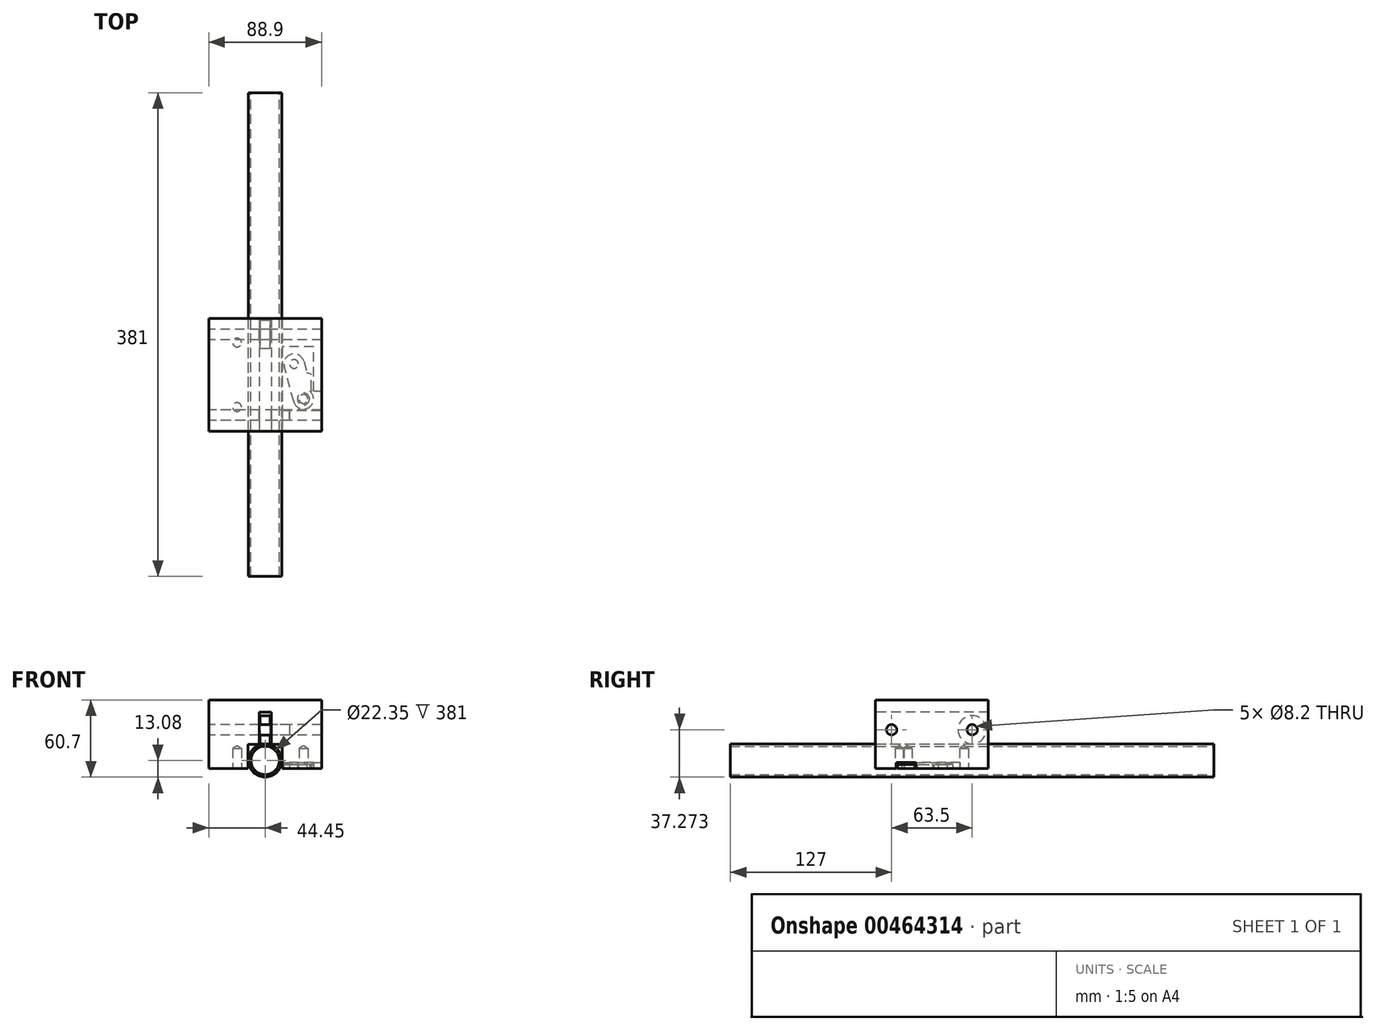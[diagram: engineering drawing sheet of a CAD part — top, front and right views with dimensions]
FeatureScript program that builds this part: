
annotation { "Feature Type Name" : "Feature", "Feature Type Description" : "" }
export const myFeature = defineFeature(function(context is Context, id is Id, definition is map)
    precondition{}
    {
        {
            var Q0;
            Q0=qCreatedBy(makeId("Front.planeOp"),FACE);
            var sketch = newSketch(context, id + "F0", { "sketchPlane" : qUnion([Q0])});
            skCircle(sketch, "E0", {"center": v(0, 0) * mm, "radius": 13.08 * mm});
            skCircle(sketch, "E1", {"center": v(0, 0) * mm, "radius": 11.18 * mm});
            skLineSegment(sketch, "E2.bottom", {"start": v(-3.94, 13.08) * mm, "end": v(3.94, 13.08) * mm});
            skLineSegment(sketch, "E2.top", {"start": v(-3.94, 20.13) * mm, "end": v(3.94, 20.13) * mm});
            skLineSegment(sketch, "E2.left", {"start": v(-3.94, 13.08) * mm, "end": v(-3.94, 20.13) * mm});
            skLineSegment(sketch, "E2.right", {"start": v(3.94, 13.08) * mm, "end": v(3.94, 20.13) * mm});
            skLineSegment(sketch, "E3", {"start": v(-8.64, 24.2) * mm, "end": v(7.29, 24.2) * mm, "construction": true});
            skLineSegment(sketch, "E4", {"start": v(0, 13.08) * mm, "end": v(0, 0) * mm, "construction": true});
            skSolve(sketch);
        }
        {
            var Q0;
            Q0=makeQuery(id+"F0.imprint","IMPRINT",FACE,{"disambiguationData":[TD([[makeQuery(id+"F0.imprint","IMPRINT",EDGE,{"derivedFrom":sQuery(id+"F0.wireOp",EDGE,"E0")}),1.0]])]});
            extrude(context, id + "F1", {"entities" : qUnion([Q0]), "depth" : 381 * mm, "symmetric" : true});
        }
        {
            var Q0;
            Q0=makeQuery(id+"F0.imprint","IMPRINT",FACE,{"disambiguationData":[TD([[makeQuery(id+"F0.imprint","IMPRINT",EDGE,{"derivedFrom":sQuery(id+"F0.wireOp",EDGE,"E2.top")}),-1.0]])]});
            var Q1;
            Q1=sQuery(id+"F0.wireOp",EDGE,"E3");
            revolve(context, id + "F2", {"entities" : qUnion([Q0]), "axis" : qUnion([Q1]), "revolveType" : RevolveType.FULL});
        }
        {
            var Q0;
            Q0=qCreatedBy(makeId("Front.planeOp"),FACE);
            var sketch = newSketch(context, id + "F3", { "sketchPlane" : qUnion([Q0])});
            skLineSegment(sketch, "E5.bottom", {"start": v(-44.45, -6.35) * mm, "end": v(44.45, -6.35) * mm});
            skLineSegment(sketch, "E5.top", {"start": v(-44.45, 47.62) * mm, "end": v(44.45, 47.62) * mm});
            skLineSegment(sketch, "E5.left", {"start": v(-44.45, -6.35) * mm, "end": v(-44.45, 47.63) * mm});
            skLineSegment(sketch, "E5.right", {"start": v(44.45, -6.35) * mm, "end": v(44.45, 47.63) * mm});
            skLineSegment(sketch, "E6.bottom", {"start": v(-4.76, 38.1) * mm, "end": v(4.76, 38.1) * mm});
            skLineSegment(sketch, "E6.top", {"start": v(-4.76, 0) * mm, "end": v(4.76, 0) * mm});
            skLineSegment(sketch, "E6.left", {"start": v(-4.76, 38.1) * mm, "end": v(-4.76, 0) * mm});
            skLineSegment(sketch, "E6.right", {"start": v(4.76, 38.1) * mm, "end": v(4.76, 0) * mm});
            skLineSegment(sketch, "E7.bottom", {"start": v(-13.46, 12.7) * mm, "end": v(13.46, 12.7) * mm});
            skLineSegment(sketch, "E7.top", {"start": v(-13.46, -14.22) * mm, "end": v(13.46, -14.22) * mm});
            skLineSegment(sketch, "E7.left", {"start": v(-13.46, 12.7) * mm, "end": v(-13.46, -14.22) * mm});
            skLineSegment(sketch, "E7.right", {"start": v(13.46, 12.7) * mm, "end": v(13.46, -14.22) * mm});
            skLineSegment(sketch, "E8", {"start": v(0, 47.62) * mm, "end": v(0, 0) * mm, "construction": true});
            skCircle(sketch, "E9.0", {"center": v(0, 0) * mm, "radius": 13.08 * mm});
            skLineSegment(sketch, "E10.bottom", {"start": v(-10.98, -7.11) * mm, "end": v(-33.2, -7.11) * mm});
            skLineSegment(sketch, "E10.top", {"start": v(-10.98, -14.99) * mm, "end": v(-33.2, -14.99) * mm});
            skLineSegment(sketch, "E10.left", {"start": v(-10.98, -7.11) * mm, "end": v(-10.98, -14.99) * mm});
            skLineSegment(sketch, "E10.right", {"start": v(-33.2, -7.11) * mm, "end": v(-33.2, -14.99) * mm});
            skLineSegment(sketch, "E11", {"start": v(-22.1, -14.99) * mm, "end": v(-22.1, 0) * mm, "construction": true});
            skSolve(sketch);
        }
        {
            var Q0;
            Q0=makeQuery(id+"F3.imprint","IMPRINT",FACE,{"disambiguationData":[TD([[makeQuery(id+"F3.imprint","IMPRINT",EDGE,{"derivedFrom":sQuery(id+"F3.wireOp",EDGE,"E5.top")}),-1.0]])]});
            extrude(context, id + "F4", {"entities" : qUnion([Q0]), "oppositeDirection" : true, "depth" : 12.7 * mm, "hasSecondDirection" : true, "secondDirectionOppositeDirection" : false, "secondDirectionDepth" : 76.2 * mm});
        }
        {
            var Q0;
            {var subQ0=sQuery(id+"F3.wireOp",EDGE,"E5.bottom");Q0=makeQuery(id+"F4.opExtrude","SWEPT_FACE",FACE,{"disambiguationData":[OSD([subQ0]),TDD([makeQuery(id+"F3.imprint","IMPRINT",EDGE,{"disambiguationData":[TD([[makeQuery(id+"F3.imprint","INTERSECT",VERTEX,{"derivedFrom":[subQ0,sQuery(id+"F3.wireOp",EDGE,"E5.left")]}),-1.0]])],"derivedFrom":subQ0})])]});}
            var sketch = newSketch(context, id + "F5", { "sketchPlane" : qUnion([Q0])});
            skPoint(sketch, "E12.0", {"position": v(-22.1, 0) * mm});
            skLineSegment(sketch, "E13", {"start": v(-22.1, 0) * mm, "end": v(-22.1, 57.15) * mm, "construction": true});
            skPoint(sketch, "E14", {"position": v(-22.1, 57.15) * mm});
            skPoint(sketch, "E15", {"position": v(-22.1, 6.35) * mm});
            skLineSegment(sketch, "E16.0", {"start": v(-44.45, 76.2) * mm, "end": v(-13.46, 76.2) * mm});
            skLineSegment(sketch, "E17.0", {"start": v(-44.45, -12.7) * mm, "end": v(-44.45, 76.2) * mm});
            skPoint(sketch, "E18", {"position": v(30.18, 50.8) * mm});
            skSolve(sketch);
        }
        {
            var Q0;
            Q0=sQuery(id+"F5.wireOp",VERTEX,"E14");
            var Q1;
            Q1=sQuery(id+"F5.wireOp",VERTEX,"E15");
            var Q2;
            Q2=sQuery(id+"F5.wireOp",VERTEX,"E18");
            var Q3;
            Q3=makeQuery(id+"F4.opExtrude","SWEPT_BODY",BODY,{"disambiguationData":[OSD([sQuery(id+"F3.wireOp",EDGE,"E5.bottom"),sQuery(id+"F3.wireOp",EDGE,"E5.top"),sQuery(id+"F3.wireOp",EDGE,"E5.left"),sQuery(id+"F3.wireOp",EDGE,"E5.right"),sQuery(id+"F3.wireOp",EDGE,"E6.bottom"),sQuery(id+"F3.wireOp",EDGE,"E6.left"),sQuery(id+"F3.wireOp",EDGE,"E6.right"),sQuery(id+"F3.wireOp",EDGE,"E7.bottom"),sQuery(id+"F3.wireOp",EDGE,"E7.left"),sQuery(id+"F3.wireOp",EDGE,"E7.right")])]});
            hole(context, id + "F6", {"style" : HoleStyle.SIMPLE, "endStyle" : HoleEndStyle.BLIND, "standardTappedOrClearance" : lookupTablePath({ "standard" : "ANSI", "engagement" : "75%", "pitch" : "24 tpi", "size" : "5/16", "type" : "Tapped" }), "standardBlindInLast" : lookupTablePath({ "standard" : "ANSI", "engagement" : "75%", "pitch" : "24 tpi", "size" : "5/16", "type" : "Tapped" }), "holeDiameter" : 6.9 * mm, "showTappedDepth" : true, "holeDepth" : 15.88 * mm, "isTappedThrough" : true, "tappedDepth" : 12.7 * mm, "tapClearance" : 3, "startFromSketch" : true, "locations" : qUnion([Q0, Q1, Q2]), "scope" : qUnion([Q3]), "majorDiameter" : 7.94 * mm});
        }
        {
            var Q0;
            Q0=makeQuery(id+"F4.opExtrude","SWEPT_FACE",FACE,{"disambiguationData":[OSD([sQuery(id+"F3.wireOp",EDGE,"E5.left")])]});
            var sketch = newSketch(context, id + "F7", { "sketchPlane" : qUnion([Q0])});
            skPoint(sketch, "E19.0", {"position": v(0, 24.2) * mm});
            skLineSegment(sketch, "E20", {"start": v(0, 24.2) * mm, "end": v(63.5, 24.2) * mm});
            skPoint(sketch, "E21", {"position": v(63.5, 24.2) * mm});
            skSolve(sketch);
        }
        {
            var Q0;
            Q0=sQuery(id+"F7.wireOp",VERTEX,"E19.0");
            var Q1;
            Q1=sQuery(id+"F7.wireOp",VERTEX,"E21");
            var Q2;
            Q2=makeQuery(id+"F4.opExtrude","SWEPT_BODY",BODY,{"disambiguationData":[OSD([sQuery(id+"F3.wireOp",EDGE,"E5.bottom"),sQuery(id+"F3.wireOp",EDGE,"E5.top"),sQuery(id+"F3.wireOp",EDGE,"E5.left"),sQuery(id+"F3.wireOp",EDGE,"E5.right"),sQuery(id+"F3.wireOp",EDGE,"E6.bottom"),sQuery(id+"F3.wireOp",EDGE,"E6.left"),sQuery(id+"F3.wireOp",EDGE,"E6.right"),sQuery(id+"F3.wireOp",EDGE,"E7.bottom"),sQuery(id+"F3.wireOp",EDGE,"E7.left"),sQuery(id+"F3.wireOp",EDGE,"E7.right")])]});
            var Q3;
            Q3=makeQuery(id+"F2.opRevolve","SWEPT_BODY",BODY,{"disambiguationData":[OSD([sQuery(id+"F0.wireOp",EDGE,"E2.bottom"),sQuery(id+"F0.wireOp",EDGE,"E2.top"),sQuery(id+"F0.wireOp",EDGE,"E2.left"),sQuery(id+"F0.wireOp",EDGE,"E2.right")])]});
            hole(context, id + "F8", {"style" : HoleStyle.SIMPLE, "endStyle" : HoleEndStyle.THROUGH, "standardTappedOrClearance" : lookupTablePath({ "standard" : "ANSI", "fit" : "Close", "size" : "5/16", "type" : "Clearance" }), "standardBlindInLast" : lookupTablePath({ "fit" : "Close", "standard" : "ANSI", "size" : "5/16", "type" : "Clearance" }), "holeDiameter" : 8.2 * mm, "isTappedThrough" : true, "tappedDepth" : 12.7 * mm, "tapClearance" : 3, "startFromSketch" : true, "locations" : qUnion([Q0, Q1]), "scope" : qUnion([Q2, Q3])});
        }
        {
            var Q0;
            Q0=makeQuery(id+"F4.opExtrude","SWEPT_FACE",FACE,{"disambiguationData":[OSD([sQuery(id+"F3.wireOp",EDGE,"E5.left")])]});
            var sketch = newSketch(context, id + "F9", { "sketchPlane" : qUnion([Q0])});
            skCircle(sketch, "E22.0", {"center": v(63.5, 24.2) * mm, "radius": 4.1 * mm});
            skSolve(sketch);
        }
        {
            var Q0;
            Q0=makeQuery(id+"F9.imprint","IMPRINT",FACE,{"disambiguationData":[TD([[makeQuery(id+"F9.imprint","IMPRINT",EDGE,{"derivedFrom":sQuery(id+"F9.wireOp",EDGE,"E22.0")}),1.0]])]});
            extrude(context, id + "F10", {"entities" : qUnion([Q0]), "oppositeDirection" : true, "depth" : 63.5 * mm});
        }
        {
            var Q0;
            {var subQ0=sQuery(id+"F3.wireOp",EDGE,"E5.bottom");Q0=makeQuery(id+"F4.opExtrude","SWEPT_FACE",FACE,{"disambiguationData":[OSD([subQ0]),TDD([makeQuery(id+"F3.imprint","IMPRINT",EDGE,{"disambiguationData":[TD([[makeQuery(id+"F3.imprint","INTERSECT",VERTEX,{"derivedFrom":[subQ0,sQuery(id+"F3.wireOp",EDGE,"E5.right")]}),1.0]])],"derivedFrom":subQ0})])]});}
            var sketch = newSketch(context, id + "F11", { "sketchPlane" : qUnion([Q0])});
            skCircle(sketch, "E23.0", {"center": v(30.18, 50.8) * mm, "radius": 3.45 * mm});
            skCircle(sketch, "E24", {"center": v(30.18, 50.8) * mm, "radius": 4.76 * mm});
            skCircle(sketch, "E25", {"center": v(30.18, 50.8) * mm, "radius": 7.94 * mm});
            skCircle(sketch, "E26", {"center": v(22.78, 23.2) * mm, "radius": 3.45 * mm});
            skCircle(sketch, "E27", {"center": v(22.78, 23.2) * mm, "radius": 7.94 * mm});
            skLineSegment(sketch, "E28", {"start": v(22.5, 52.85) * mm, "end": v(15.11, 25.25) * mm});
            skLineSegment(sketch, "E29", {"start": v(30.45, 21.14) * mm, "end": v(37.84, 48.75) * mm});
            skLineSegment(sketch, "E30", {"start": v(36.39, 43.31) * mm, "end": v(36.39, 31.04) * mm});
            skLineSegment(sketch, "E31", {"start": v(36.39, 31.04) * mm, "end": v(32.84, 30.1) * mm});
            skLineSegment(sketch, "E32", {"start": v(37.84, 48.75) * mm, "end": v(39.21, 48.38) * mm, "construction": true});
            skLineSegment(sketch, "E33.0.0", {"start": v(44.45, 76.2) * mm, "end": v(13.46, 76.2) * mm});
            skLineSegment(sketch, "E33.0.1", {"start": v(13.46, 76.2) * mm, "end": v(13.46, -12.7) * mm});
            skLineSegment(sketch, "E33.0.2", {"start": v(13.46, -12.7) * mm, "end": v(44.45, -12.7) * mm});
            skLineSegment(sketch, "E33.0.3", {"start": v(44.45, -12.7) * mm, "end": v(44.45, 76.2) * mm});
            skLineSegment(sketch, "E34.bottom", {"start": v(13.46, 59.69) * mm, "end": v(44.45, 59.69) * mm});
            skLineSegment(sketch, "E34.top", {"start": v(13.46, 44.45) * mm, "end": v(44.45, 44.45) * mm});
            skLineSegment(sketch, "E34.left", {"start": v(13.46, 59.7) * mm, "end": v(13.46, 44.45) * mm});
            skLineSegment(sketch, "E34.right", {"start": v(44.45, 59.69) * mm, "end": v(44.45, 44.45) * mm});
            skLineSegment(sketch, "E35.bottom", {"start": v(38.1, 44.45) * mm, "end": v(13.46, 44.45) * mm});
            skLineSegment(sketch, "E35.top", {"start": v(38.1, 9.52) * mm, "end": v(13.46, 9.52) * mm});
            skLineSegment(sketch, "E35.left", {"start": v(38.1, 44.45) * mm, "end": v(38.1, 9.52) * mm});
            skLineSegment(sketch, "E35.right", {"start": v(13.46, 44.45) * mm, "end": v(13.46, 9.52) * mm});
            skSolve(sketch);
        }
        {
            var Q0;
            Q0=makeQuery(id+"F11.imprint","IMPRINT",FACE,{"disambiguationData":[TD([[makeQuery(id+"F11.imprint","IMPRINT",EDGE,{"derivedFrom":sQuery(id+"F11.wireOp",EDGE,"E34.bottom")}),-1.0]])]});
            var Q1;
            Q1=makeQuery(id+"F11.imprint","IMPRINT",FACE,{"disambiguationData":[TD([[makeQuery(id+"F11.imprint","IMPRINT",EDGE,{"derivedFrom":sQuery(id+"F11.wireOp",EDGE,"E24")}),-1.0]])]});
            var Q2;
            {var subQ0=sQuery(id+"F11.wireOp",EDGE,"E28");var subQ1=sQuery(id+"F11.wireOp",EDGE,"E25");var subQ2=makeQuery(id+"F11.imprint","INTERSECT",VERTEX,{"derivedFrom":[subQ1,subQ0]});Q2=makeQuery(id+"F11.imprint","IMPRINT",FACE,{"disambiguationData":[TD([[makeQuery(id+"F11.imprint","IMPRINT",EDGE,{"disambiguationData":[TD([[subQ2,-1.0]])],"derivedFrom":subQ1}),-1.0]])]});}
            var Q3;
            {var subQ0=sQuery(id+"F11.wireOp",EDGE,"E29");var subQ1=sQuery(id+"F11.wireOp",EDGE,"E25");var subQ2=makeQuery(id+"F11.imprint","INTERSECT",VERTEX,{"derivedFrom":[subQ1,subQ0]});Q3=makeQuery(id+"F11.imprint","IMPRINT",FACE,{"disambiguationData":[TD([[makeQuery(id+"F11.imprint","IMPRINT",EDGE,{"disambiguationData":[TD([[subQ2,1.0]])],"derivedFrom":subQ1}),-1.0]])]});}
            var Q4;
            {var subQ6=sQuery(id+"F11.wireOp",EDGE,"E35.bottom");var subQ8=sQuery(id+"F11.wireOp",EDGE,"E25");var subQ9=makeQuery(id+"F11.imprint","INTERSECT",VERTEX,{"disambiguationData":[OD(0.0)],"derivedFrom":[subQ8,subQ6]});Q4=makeQuery(id+"F11.imprint","IMPRINT",FACE,{"disambiguationData":[TD([[makeQuery(id+"F11.imprint","IMPRINT",EDGE,{"disambiguationData":[TD([[subQ9,-1.0]])],"derivedFrom":subQ8}),-1.0]])]});}
            var Q5;
            {var subQ0=sQuery(id+"F11.wireOp",EDGE,"E35.bottom");var subQ1=sQuery(id+"F11.wireOp",EDGE,"E25");var subQ2=makeQuery(id+"F11.imprint","INTERSECT",VERTEX,{"disambiguationData":[OD(0.0)],"derivedFrom":[subQ1,subQ0]});Q5=makeQuery(id+"F11.imprint","IMPRINT",FACE,{"disambiguationData":[TD([[makeQuery(id+"F11.imprint","IMPRINT",EDGE,{"disambiguationData":[TD([[subQ2,-1.0]])],"derivedFrom":subQ1}),1.0]])]});}
            var Q6;
            {var subQ0=sQuery(id+"F11.wireOp",EDGE,"E30");Q6=makeQuery(id+"F11.imprint","IMPRINT",FACE,{"disambiguationData":[TD([[makeQuery(id+"F11.imprint","IMPRINT",EDGE,{"derivedFrom":subQ0}),-1.0]])]});}
            var Q7;
            {var subQ8=sQuery(id+"F11.wireOp",EDGE,"E30");Q7=makeQuery(id+"F11.imprint","IMPRINT",FACE,{"disambiguationData":[TD([[makeQuery(id+"F11.imprint","IMPRINT",EDGE,{"derivedFrom":subQ8}),1.0]])]});}
            var Q8;
            Q8=makeQuery(id+"F11.imprint","IMPRINT",FACE,{"disambiguationData":[TD([[makeQuery(id+"F11.imprint","IMPRINT",EDGE,{"derivedFrom":sQuery(id+"F11.wireOp",EDGE,"E26")}),-1.0]])]});
            var Q9;
            Q9=makeQuery(id+"F11.imprint","IMPRINT",FACE,{"disambiguationData":[TD([[makeQuery(id+"F11.imprint","IMPRINT",EDGE,{"derivedFrom":sQuery(id+"F11.wireOp",EDGE,"E26")}),1.0]])]});
            var Q10;
            Q10=makeQuery(id+"F11.imprint","IMPRINT",FACE,{"disambiguationData":[TD([[makeQuery(id+"F11.imprint","IMPRINT",EDGE,{"derivedFrom":sQuery(id+"F11.wireOp",EDGE,"E23.0")}),-1.0]])]});
            extrude(context, id + "F12", {"entities" : qUnion([Q0, Q1, Q2, Q3, Q4, Q5, Q6, Q7, Q8, Q9, Q10]), "operationType" : NewBodyOperationType.REMOVE, "oppositeDirection" : true, "depth" : 4.78 * mm});
        }
        {
            var Q0;
            Q0=makeQuery(id+"F11.imprint","IMPRINT",FACE,{"disambiguationData":[TD([[makeQuery(id+"F11.imprint","IMPRINT",EDGE,{"derivedFrom":sQuery(id+"F11.wireOp",EDGE,"E26")}),-1.0]])]});
            var Q1;
            {var subQ0=sQuery(id+"F11.wireOp",EDGE,"E28");var subQ1=sQuery(id+"F11.wireOp",EDGE,"E27");var subQ2=makeQuery(id+"F11.imprint","INTERSECT",VERTEX,{"derivedFrom":[subQ1,subQ0]});Q1=makeQuery(id+"F11.imprint","IMPRINT",FACE,{"disambiguationData":[TD([[makeQuery(id+"F11.imprint","IMPRINT",EDGE,{"disambiguationData":[TD([[subQ2,1.0]])],"derivedFrom":subQ1}),-1.0]])]});}
            var Q2;
            {var subQ5=sQuery(id+"F11.wireOp",EDGE,"E31");Q2=makeQuery(id+"F11.imprint","IMPRINT",FACE,{"disambiguationData":[TD([[makeQuery(id+"F11.imprint","IMPRINT",EDGE,{"derivedFrom":subQ5}),-1.0]])]});}
            var Q3;
            {var subQ0=sQuery(id+"F11.wireOp",EDGE,"E28");var subQ1=sQuery(id+"F11.wireOp",EDGE,"E25");var subQ2=makeQuery(id+"F11.imprint","INTERSECT",VERTEX,{"derivedFrom":[subQ1,subQ0]});Q3=makeQuery(id+"F11.imprint","IMPRINT",FACE,{"disambiguationData":[TD([[makeQuery(id+"F11.imprint","IMPRINT",EDGE,{"disambiguationData":[TD([[subQ2,-1.0]])],"derivedFrom":subQ1}),-1.0]])]});}
            var Q4;
            Q4=makeQuery(id+"F11.imprint","IMPRINT",FACE,{"disambiguationData":[TD([[makeQuery(id+"F11.imprint","IMPRINT",EDGE,{"derivedFrom":sQuery(id+"F11.wireOp",EDGE,"E24")}),-1.0]])]});
            var Q5;
            {var subQ0=sQuery(id+"F11.wireOp",EDGE,"E35.bottom");var subQ1=sQuery(id+"F11.wireOp",EDGE,"E25");var subQ2=makeQuery(id+"F11.imprint","INTERSECT",VERTEX,{"disambiguationData":[OD(0.0)],"derivedFrom":[subQ1,subQ0]});Q5=makeQuery(id+"F11.imprint","IMPRINT",FACE,{"disambiguationData":[TD([[makeQuery(id+"F11.imprint","IMPRINT",EDGE,{"disambiguationData":[TD([[subQ2,-1.0]])],"derivedFrom":subQ1}),1.0]])]});}
            extrude(context, id + "F13", {"entities" : qUnion([Q0, Q1, Q2, Q3, Q4, Q5]), "oppositeDirection" : true, "depth" : 3.17 * mm});
        }
    });
